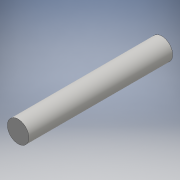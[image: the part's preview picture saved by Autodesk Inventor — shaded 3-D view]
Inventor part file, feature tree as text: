
AUTODESK INVENTOR PART (.ipt)
format: ipt  version: 2016 (Build 200138000, 138)  size: 87,040 bytes
history: native  units: mm
features: extrude x1, sketch x1
ambient origin geometry x8: Origin, YZ Plane, XZ Plane, XY Plane, X Axis, Y Axis, Z Axis, Center Point
bodies: Solid1 (feature_tree)
feature tree (2):
  extrude  "Extrusion1"  Depth=10.0mm TaperAngle=0.0deg
  sketch  "Sketch1"  dims[d0=1.5mm d1=10.0mm d2=0.0mm]
